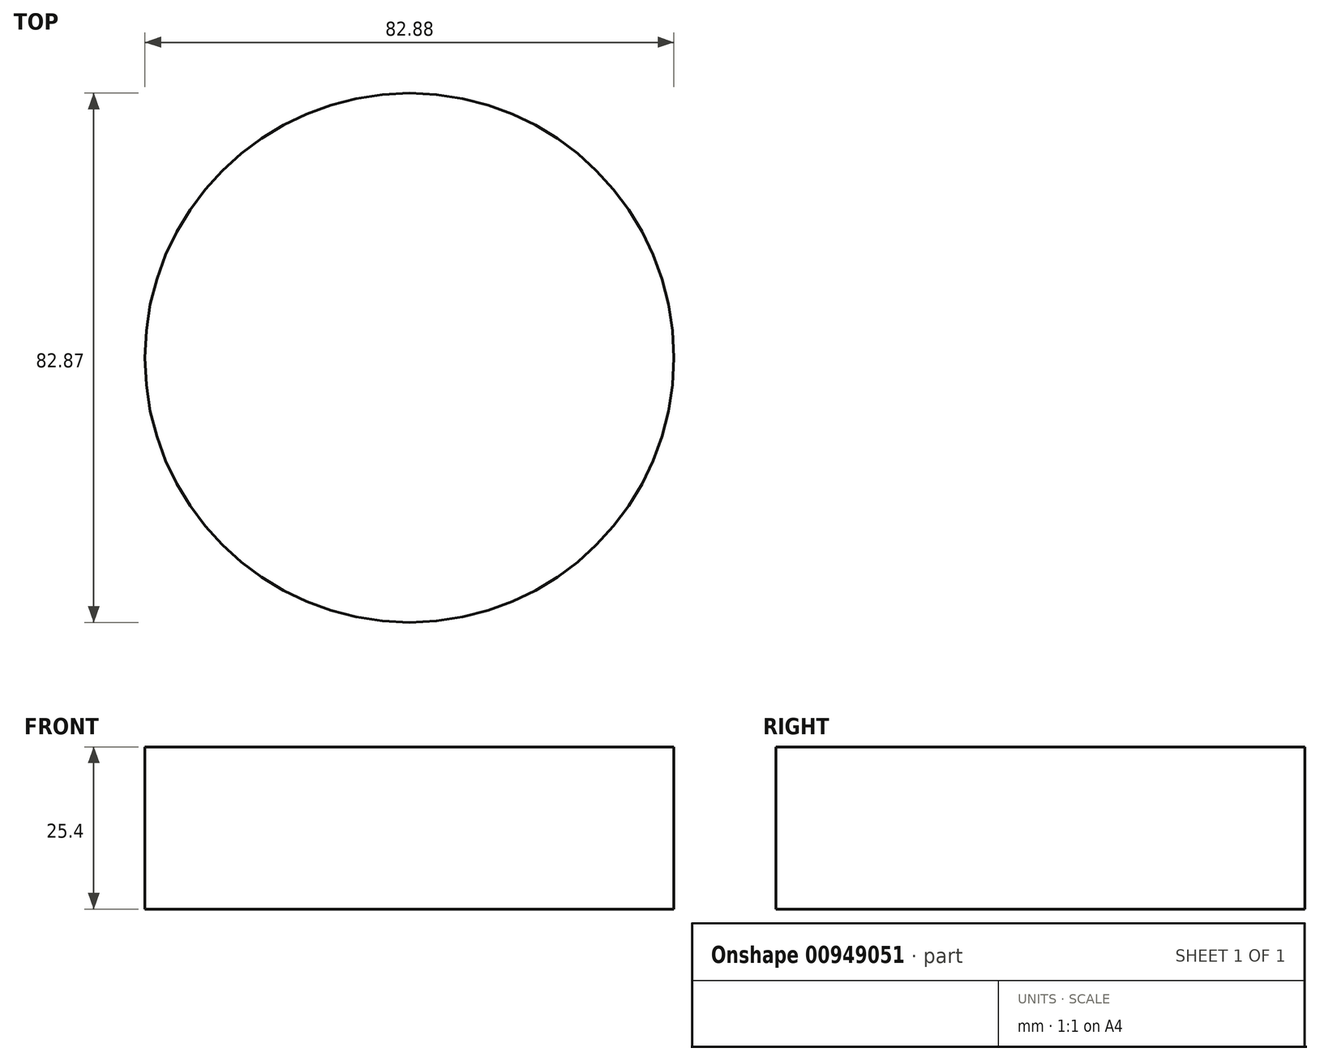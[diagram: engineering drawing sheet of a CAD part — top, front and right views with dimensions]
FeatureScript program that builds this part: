
annotation { "Feature Type Name" : "Feature", "Feature Type Description" : "" }
export const myFeature = defineFeature(function(context is Context, id is Id, definition is map)
    precondition{}
    {
        {
            var Q0;
            Q0=qCreatedBy(makeId("Top.planeOp"),FACE);
            var sketch = newSketch(context, id + "F0", { "sketchPlane" : qUnion([Q0])});
            skCircle(sketch, "E0", {"center": v(0, -35.35) * mm, "radius": 41.44 * mm});
            skSolve(sketch);
        }
        {
            var Q0;
            Q0=makeQuery(id+"F0.imprint","IMPRINT",FACE,{"disambiguationData":[TD([[makeQuery(id+"F0.imprint","IMPRINT",EDGE,{"derivedFrom":sQuery(id+"F0.wireOp",EDGE,"E0")}),1.0]])]});
            extrude(context, id + "F1", {"entities" : qUnion([Q0]), "depth" : 25.4 * mm, "offsetDistance" : 25.4 * mm});
        }
    });
